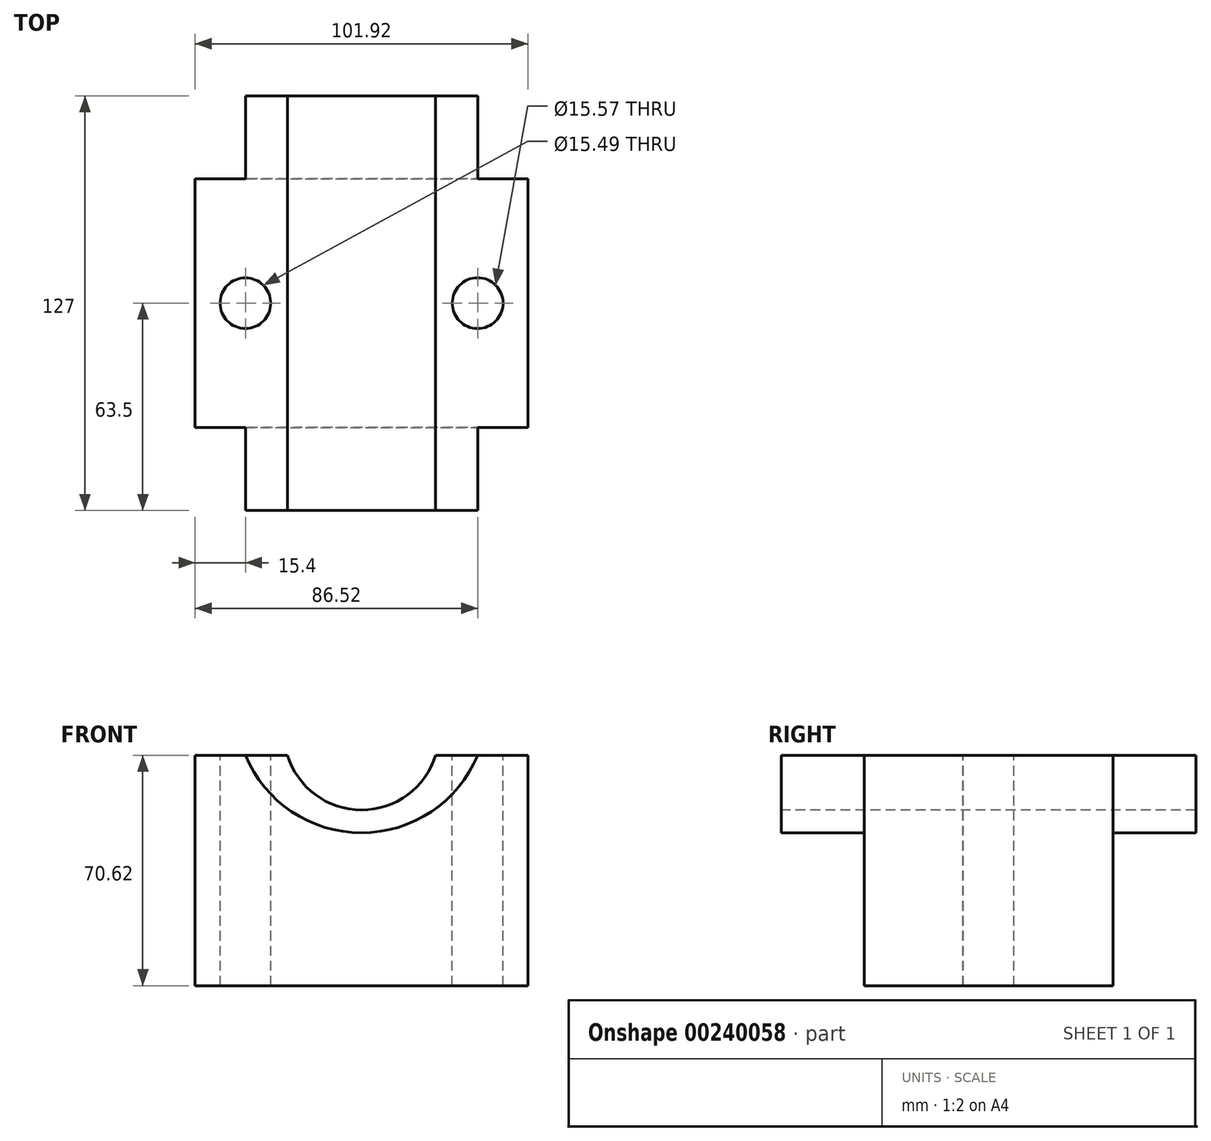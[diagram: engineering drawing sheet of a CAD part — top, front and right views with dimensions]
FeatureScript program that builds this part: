
annotation { "Feature Type Name" : "Feature", "Feature Type Description" : "" }
export const myFeature = defineFeature(function(context is Context, id is Id, definition is map)
    precondition{}
    {
        {
            var Q0;
            Q0=qCreatedBy(makeId("Front.planeOp"),FACE);
            var sketch = newSketch(context, id + "F0", { "sketchPlane" : qUnion([Q0])});
            skLineSegment(sketch, "E0.bottom", {"start": v(50.96, -35.31) * mm, "end": v(-50.96, -35.31) * mm});
            skLineSegment(sketch, "E0.top", {"start": v(50.96, 35.31) * mm, "end": v(22.65, 35.31) * mm});
            skLineSegment(sketch, "E0.left", {"start": v(50.96, -35.31) * mm, "end": v(50.96, 35.31) * mm});
            skLineSegment(sketch, "E0.right", {"start": v(-50.96, -35.31) * mm, "end": v(-50.96, 35.31) * mm});
            skPoint(sketch, "E0.middle", {"position": v(0, 0) * mm});
            skLineSegment(sketch, "E1", {"start": v(0, -2.23) * mm, "end": v(0, 35.31) * mm, "construction": true});
            skLineSegment(sketch, "E2.MirrorCS", {"start": v(-22.65, 35.31) * mm, "end": v(-35.56, 35.31) * mm});
            skArc(sketch, "E3", {"start": v(-35.56, 35.31) * mm, "mid": v(0, 11.51) * mm, "end": v(35.56, 35.31) * mm});
            skPoint(sketch, "E4.orphan", {"position": v(0, 35.31) * mm});
            skLineSegment(sketch, "E5.trimOffspring", {"start": v(-35.56, 35.31) * mm, "end": v(-50.96, 35.31) * mm});
            skPoint(sketch, "E6.MirrorCS.start.orphan", {"position": v(35.56, 35.31) * mm});
            skArc(sketch, "E7", {"start": v(-22.65, 35.31) * mm, "mid": v(0, 18.5) * mm, "end": v(22.65, 35.31) * mm});
            skSolve(sketch);
        }
        {
            var Q0;
            Q0=makeQuery(id+"F0.imprint","IMPRINT",FACE,{"disambiguationData":[TD([[makeQuery(id+"F0.imprint","IMPRINT",EDGE,{"derivedFrom":sQuery(id+"F0.wireOp",EDGE,"E0.bottom")}),-1.0]])]});
            extrude(context, id + "F1", {"entities" : qUnion([Q0]), "depth" : 76.2 * mm});
        }
        {
            var Q0;
            Q0=makeQuery(id+"F0.imprint","IMPRINT",FACE,{"disambiguationData":[TD([[makeQuery(id+"F0.imprint","IMPRINT",EDGE,{"derivedFrom":sQuery(id+"F0.wireOp",EDGE,"E2.MirrorCS")}),1.0]])]});
            extrude(context, id + "F2", {"entities" : qUnion([Q0]), "operationType" : NewBodyOperationType.ADD, "oppositeDirection" : true, "depth" : 25.4 * mm, "hasSecondDirection" : true, "secondDirectionOppositeDirection" : false, "secondDirectionDepth" : 101.6 * mm});
        }
        {
            var Q0;
            {var subQ0=sQuery(id+"F0.wireOp",EDGE,"E0.top");Q0=makeQuery(id+"F2.boolean.opBoolean","MERGE",FACE,{"derivedFrom":[makeQuery(id+"F1.opExtrude","SWEPT_FACE",FACE,{"disambiguationData":[OSD([subQ0])]}),makeQuery(id+"F2.opExtrude","SWEPT_FACE",FACE,{"disambiguationData":[OSD([subQ0])]})]});}
            var sketch = newSketch(context, id + "F3", { "sketchPlane" : qUnion([Q0])});
            skLineSegment(sketch, "E8", {"start": v(35.56, 0) * mm, "end": v(35.56, -76.2) * mm, "construction": true});
            skCircle(sketch, "E9", {"center": v(35.56, -38.1) * mm, "radius": 7.79 * mm});
            skSolve(sketch);
        }
        {
            var Q0;
            Q0=makeQuery(id+"F3.imprint","IMPRINT",FACE,{"disambiguationData":[TD([[makeQuery(id+"F3.imprint","IMPRINT",EDGE,{"derivedFrom":sQuery(id+"F3.wireOp",EDGE,"E9")}),1.0]])]});
            extrude(context, id + "F4", {"entities" : qUnion([Q0]), "operationType" : NewBodyOperationType.REMOVE, "oppositeDirection" : true, "depth" : 101.6 * mm});
        }
        {
            var Q0;
            Q0=makeQuery(id+"F2.boolean.opBoolean","MERGE",FACE,{"derivedFrom":[makeQuery(id+"F1.opExtrude","SWEPT_FACE",FACE,{"disambiguationData":[OSD([sQuery(id+"F0.wireOp",EDGE,"E5.trimOffspring")])]}),makeQuery(id+"F2.opExtrude","SWEPT_FACE",FACE,{"disambiguationData":[OSD([sQuery(id+"F0.wireOp",EDGE,"E2.MirrorCS")])]})]});
            var sketch = newSketch(context, id + "F5", { "sketchPlane" : qUnion([Q0])});
            skLineSegment(sketch, "E10", {"start": v(-35.56, 0) * mm, "end": v(-35.56, -76.2) * mm, "construction": true});
            skCircle(sketch, "E11", {"center": v(-35.56, -38.1) * mm, "radius": 7.75 * mm});
            skSolve(sketch);
        }
        {
            var Q0;
            Q0=makeQuery(id+"F5.imprint","IMPRINT",FACE,{"disambiguationData":[TD([[makeQuery(id+"F5.imprint","IMPRINT",EDGE,{"derivedFrom":sQuery(id+"F5.wireOp",EDGE,"E11")}),1.0]])]});
            extrude(context, id + "F6", {"entities" : qUnion([Q0]), "operationType" : NewBodyOperationType.REMOVE, "oppositeDirection" : true, "depth" : 101.6 * mm});
        }
    });
